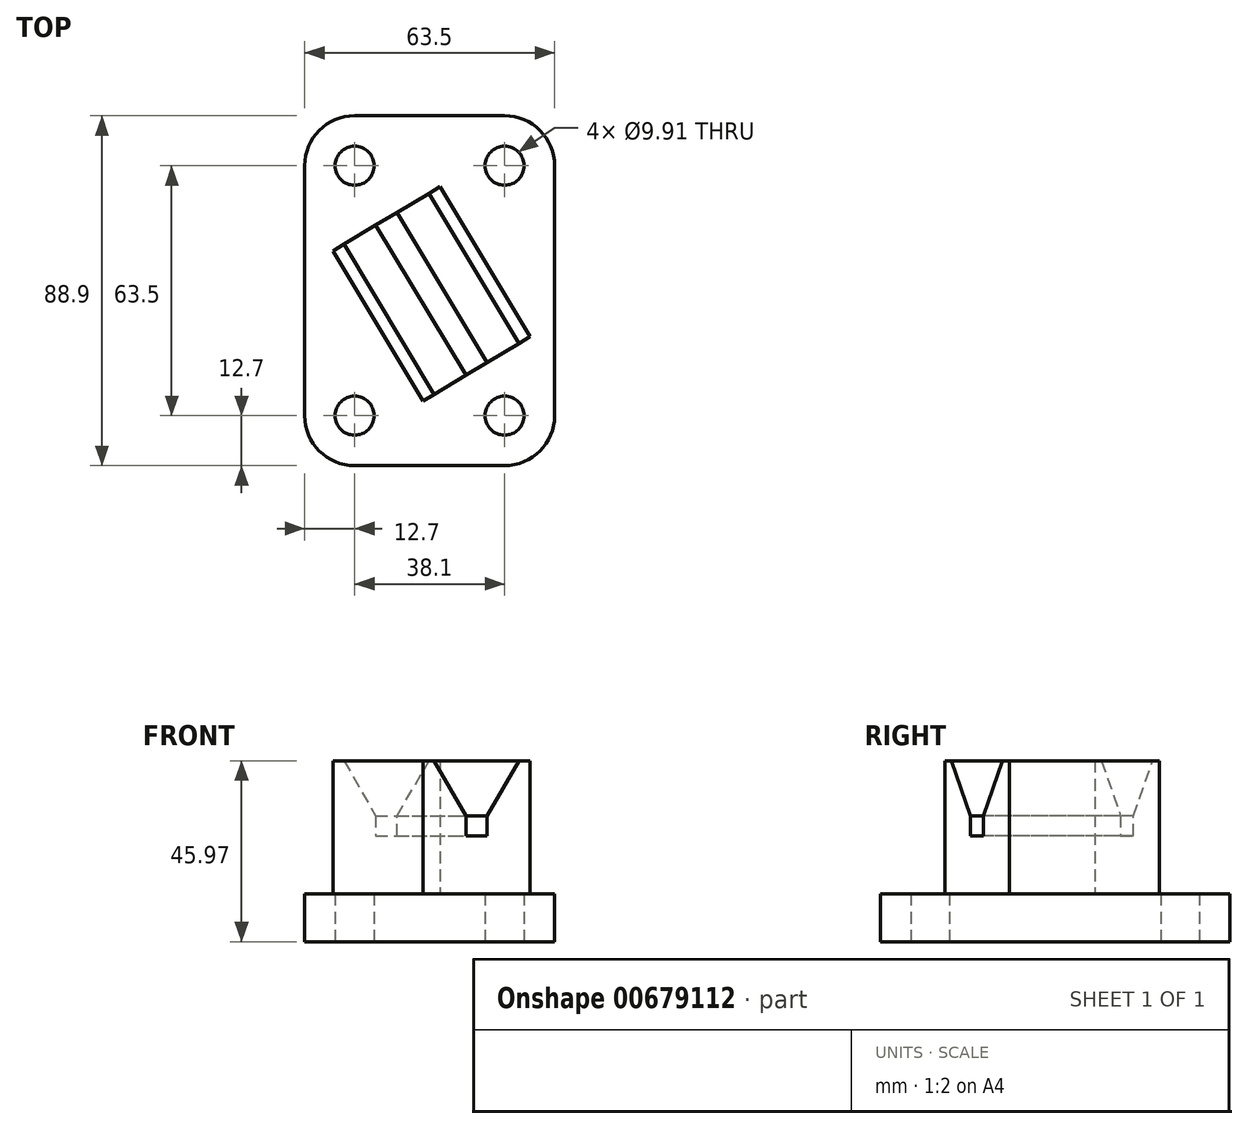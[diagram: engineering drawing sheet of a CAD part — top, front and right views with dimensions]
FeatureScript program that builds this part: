
annotation { "Feature Type Name" : "Feature", "Feature Type Description" : "" }
export const myFeature = defineFeature(function(context is Context, id is Id, definition is map)
    precondition{}
    {
        {
            var Q0;
            Q0=qCreatedBy(makeId("Top.planeOp"),FACE);
            var sketch = newSketch(context, id + "F0", { "sketchPlane" : qUnion([Q0])});
            skLineSegment(sketch, "E0.bottom", {"start": v(12.7, 0) * mm, "end": v(50.8, 0) * mm});
            skLineSegment(sketch, "E0.top", {"start": v(12.7, 88.9) * mm, "end": v(50.8, 88.9) * mm});
            skLineSegment(sketch, "E0.left", {"start": v(0, 12.7) * mm, "end": v(0, 76.2) * mm});
            skLineSegment(sketch, "E0.right", {"start": v(63.5, 12.7) * mm, "end": v(63.5, 76.2) * mm});
            skPoint(sketch, "E1.visualSharp", {"position": v(0, 88.9) * mm});
            skArc(sketch, "E1.filletArc", {"start": v(12.7, 88.9) * mm, "mid": v(3.72, 85.18) * mm, "end": v(0, 76.2) * mm});
            skPoint(sketch, "E2.visualSharp", {"position": v(63.5, 88.9) * mm});
            skArc(sketch, "E2.filletArc", {"start": v(63.5, 76.2) * mm, "mid": v(59.78, 85.18) * mm, "end": v(50.8, 88.9) * mm});
            skPoint(sketch, "E3.visualSharp", {"position": v(0, 0) * mm});
            skArc(sketch, "E3.filletArc", {"start": v(0, 12.7) * mm, "mid": v(3.72, 3.72) * mm, "end": v(12.7, 0) * mm});
            skPoint(sketch, "E4.visualSharp", {"position": v(63.5, 0) * mm});
            skArc(sketch, "E4.filletArc", {"start": v(50.8, 0) * mm, "mid": v(59.78, 3.72) * mm, "end": v(63.5, 12.7) * mm});
            skLineSegment(sketch, "E5", {"start": v(57.27, 32.77) * mm, "end": v(30.05, 16.43) * mm});
            skLineSegment(sketch, "E6", {"start": v(57.27, 32.77) * mm, "end": v(34.4, 70.88) * mm});
            skLineSegment(sketch, "E7", {"start": v(7.18, 54.55) * mm, "end": v(30.05, 16.43) * mm});
            skLineSegment(sketch, "E8", {"start": v(34.4, 70.88) * mm, "end": v(7.18, 54.55) * mm});
            skLineSegment(sketch, "E9", {"start": v(8.4, 73.74) * mm, "end": v(8.5, 73.56) * mm});
            skCircle(sketch, "E10", {"center": v(12.7, 76.2) * mm, "radius": 4.95 * mm});
            skCircle(sketch, "E11", {"center": v(50.8, 76.2) * mm, "radius": 4.95 * mm});
            skCircle(sketch, "E12", {"center": v(50.8, 12.7) * mm, "radius": 4.95 * mm});
            skCircle(sketch, "E13", {"center": v(12.7, 12.7) * mm, "radius": 4.95 * mm});
            skSolve(sketch);
        }
        {
            var Q0;
            Q0=makeQuery(id+"F0.imprint","IMPRINT",FACE,{"disambiguationData":[TD([[makeQuery(id+"F0.imprint","IMPRINT",EDGE,{"derivedFrom":sQuery(id+"F0.wireOp",EDGE,"E0.bottom")}),1.0]])]});
            extrude(context, id + "F1", {"entities" : qUnion([Q0]), "depth" : 12.2 * mm, "offsetDistance" : 25.4 * mm});
        }
        {
            var Q0;
            Q0=makeQuery(id+"F0.imprint","IMPRINT",FACE,{"disambiguationData":[TD([[makeQuery(id+"F0.imprint","IMPRINT",EDGE,{"derivedFrom":sQuery(id+"F0.wireOp",EDGE,"E5")}),-1.0]])]});
            extrude(context, id + "F2", {"entities" : qUnion([Q0]), "operationType" : NewBodyOperationType.ADD, "depth" : 45.97 * mm, "offsetDistance" : 25.4 * mm});
        }
        {
            var Q0;
            Q0=makeQuery(id+"F2.opExtrude","SWEPT_FACE",FACE,{"disambiguationData":[OSD([sQuery(id+"F0.wireOp",EDGE,"E5")])]});
            var sketch = newSketch(context, id + "F3", { "sketchPlane" : qUnion([Q0])});
            skLineSegment(sketch, "E14", {"start": v(34.22, 12.2) * mm, "end": v(34.22, 45.97) * mm});
            skLineSegment(sketch, "E15", {"start": v(34.22, 45.97) * mm, "end": v(37.52, 45.97) * mm});
            skLineSegment(sketch, "E16", {"start": v(37.52, 45.97) * mm, "end": v(46.92, 32) * mm});
            skLineSegment(sketch, "E17", {"start": v(46.92, 32) * mm, "end": v(46.92, 26.92) * mm});
            skLineSegment(sketch, "E18", {"start": v(46.92, 26.92) * mm, "end": v(53.27, 26.92) * mm});
            skLineSegment(sketch, "E19", {"start": v(53.27, 26.92) * mm, "end": v(53.27, 32) * mm});
            skLineSegment(sketch, "E20", {"start": v(53.27, 32) * mm, "end": v(62.67, 45.97) * mm});
            skLineSegment(sketch, "E21", {"start": v(62.67, 45.97) * mm, "end": v(65.97, 45.97) * mm});
            skLineSegment(sketch, "E22", {"start": v(65.97, 45.97) * mm, "end": v(65.97, 12.2) * mm});
            skLineSegment(sketch, "E23", {"start": v(65.97, 12.2) * mm, "end": v(34.22, 12.2) * mm});
            skSolve(sketch);
        }
        {
            var Q0;
            {var subQ0=sQuery(id+"F3.wireOp",EDGE,"E16");Q0=makeQuery(id+"F3.imprint","IMPRINT",FACE,{"disambiguationData":[TD([[makeQuery(id+"F3.imprint","IMPRINT",EDGE,{"derivedFrom":subQ0}),1.0]])]});}
            extrude(context, id + "F4", {"entities" : qUnion([Q0]), "operationType" : NewBodyOperationType.REMOVE, "endBound" : BoundingType.THROUGH_ALL, "oppositeDirection" : true, "depth" : 40.13 * mm, "offsetDistance" : 25.4 * mm});
        }
    });
